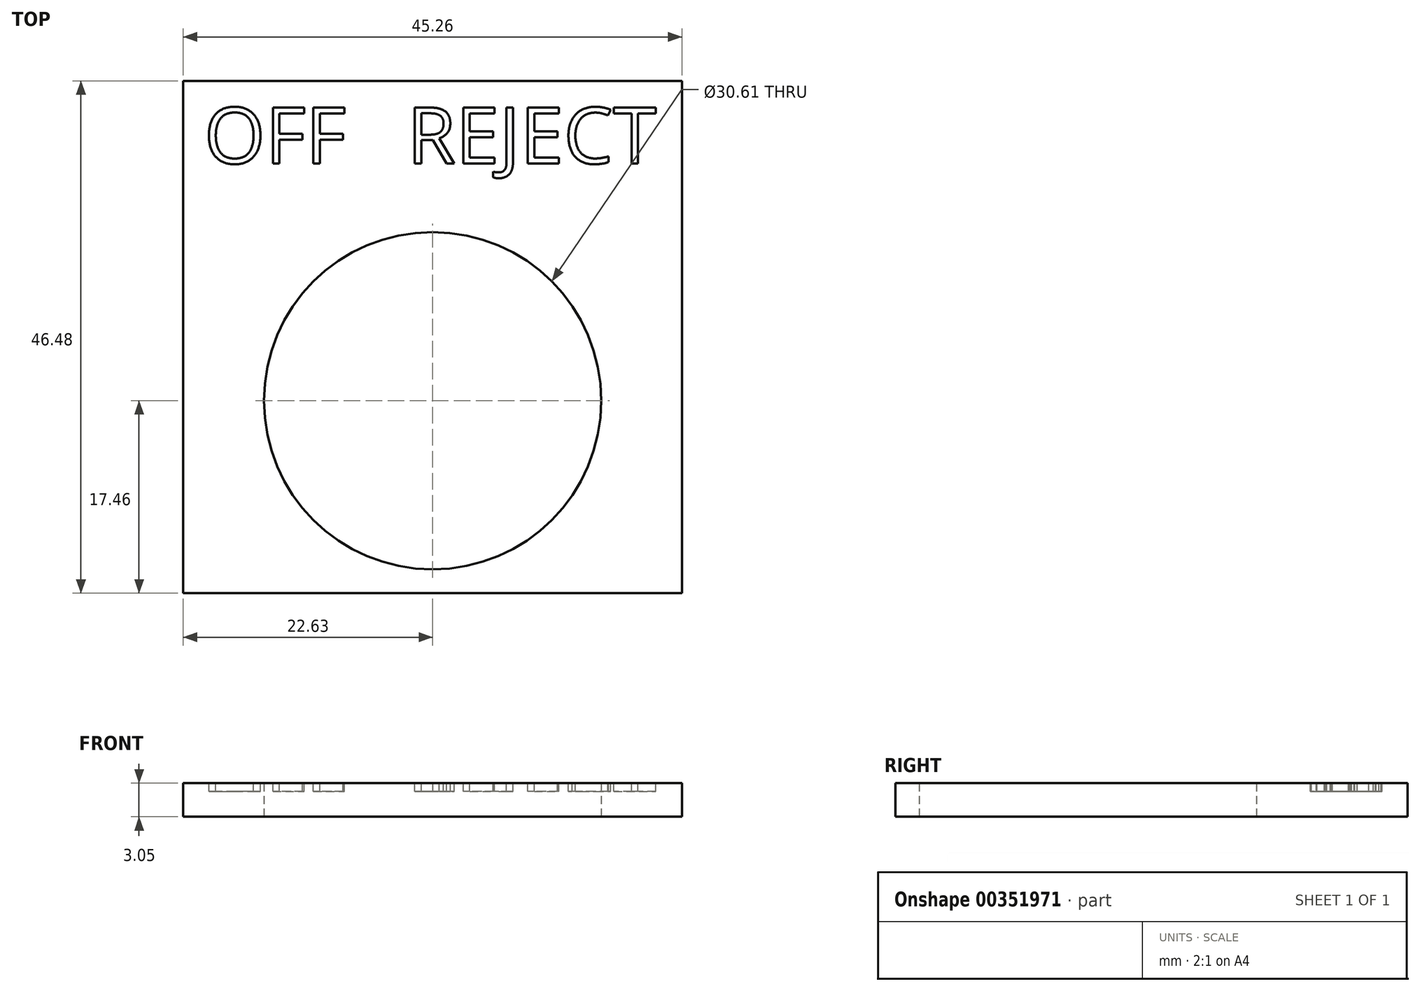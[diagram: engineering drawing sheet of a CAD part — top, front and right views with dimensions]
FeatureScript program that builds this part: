
annotation { "Feature Type Name" : "Feature", "Feature Type Description" : "" }
export const myFeature = defineFeature(function(context is Context, id is Id, definition is map)
    precondition{}
    {
        {
            var Q0;
            Q0=qCreatedBy(makeId("Top.planeOp"),FACE);
            var sketch = newSketch(context, id + "F0", { "sketchPlane" : qUnion([Q0])});
            skLineSegment(sketch, "E0.bottom", {"start": v(-22.63, -17.46) * mm, "end": v(22.63, -17.46) * mm});
            skLineSegment(sketch, "E0.top", {"start": v(-22.63, 29.02) * mm, "end": v(22.63, 29.02) * mm});
            skLineSegment(sketch, "E0.left", {"start": v(-22.63, -17.46) * mm, "end": v(-22.63, 29.02) * mm});
            skLineSegment(sketch, "E0.right", {"start": v(22.63, -17.46) * mm, "end": v(22.63, 29.02) * mm});
            skCircle(sketch, "E1", {"center": v(0, 0) * mm, "radius": 15.3 * mm});
            skLineSegment(sketch, "E2", {"start": v(0, 0) * mm, "end": v(-22.63, 0) * mm, "construction": true});
            skLineSegment(sketch, "E3", {"start": v(0, 0) * mm, "end": v(0, -17.46) * mm, "construction": true});
            skSolve(sketch);
        }
        {
            var Q0;
            Q0=makeQuery(id+"F0.imprint","IMPRINT",FACE,{"disambiguationData":[TD([[makeQuery(id+"F0.imprint","IMPRINT",EDGE,{"derivedFrom":sQuery(id+"F0.wireOp",EDGE,"E0.bottom")}),1.0]])]});
            extrude(context, id + "F1", {"entities" : qUnion([Q0]), "depth" : 3.05 * mm});
        }
        {
            var Q0;
            Q0=makeQuery(id+"F1.opExtrude","CAP_FACE",FACE,{"disambiguationData":[OSD([sQuery(id+"F0.wireOp",EDGE,"E0.bottom"),sQuery(id+"F0.wireOp",EDGE,"E0.top"),sQuery(id+"F0.wireOp",EDGE,"E0.left"),sQuery(id+"F0.wireOp",EDGE,"E0.right"),sQuery(id+"F0.wireOp",EDGE,"E1")])],"isStart":false});
            var sketch = newSketch(context, id + "F2", { "sketchPlane" : qUnion([Q0])});
            skText(sketch, "E4", { "text": "OFF   REJECT", "fontName": "OpenSans-Regular.ttf"});
            skPoint(sketch, "E5", {"position": v(0, 29.02) * mm});
            const initialGuessF2  = {"E4": [-0.02073, 0.02153, 1, 0, 0.00512]};
            skSetInitialGuess(sketch, initialGuessF2);
            skSolve(sketch);
        }
        {
            var Q0;
            Q0 = qSketchRegion(id + "F2", true);
            extrude(context, id + "F3", {"entities" : qUnion([Q0]), "operationType" : NewBodyOperationType.REMOVE, "oppositeDirection" : true, "depth" : 0.76 * mm});
        }
    });
